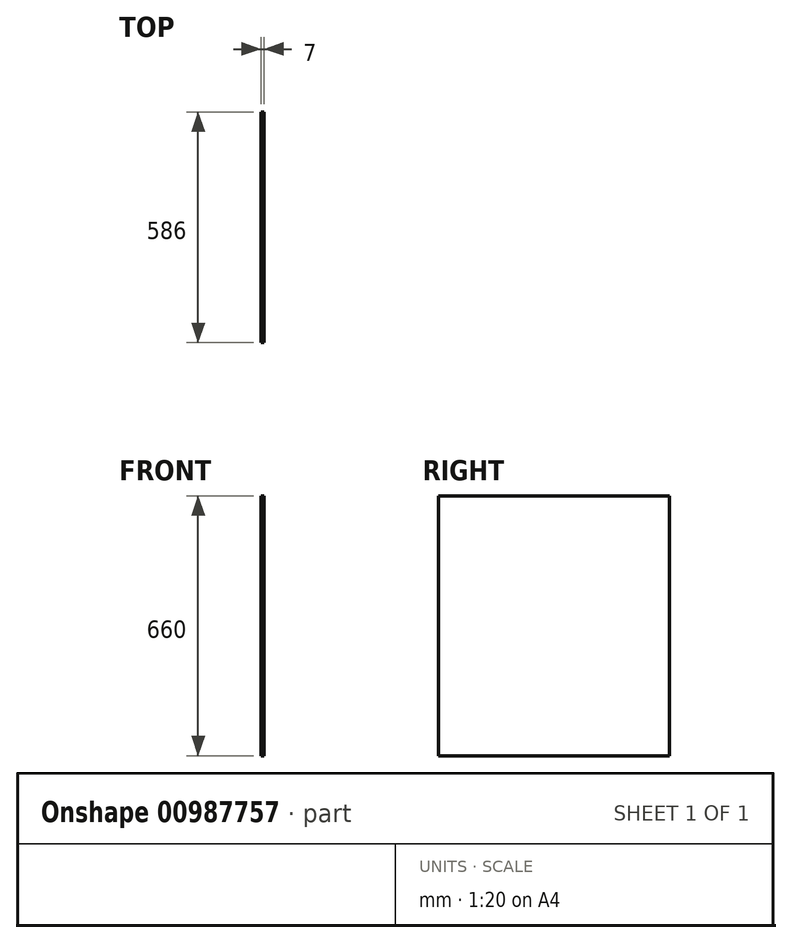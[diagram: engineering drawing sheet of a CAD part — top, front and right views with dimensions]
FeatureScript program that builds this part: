
annotation { "Feature Type Name" : "Feature", "Feature Type Description" : "" }
export const myFeature = defineFeature(function(context is Context, id is Id, definition is map)
    precondition{}
    {
        {
            var Q0;
            Q0=qCreatedBy(makeId("Right.planeOp"),FACE);
            var sketch = newSketch(context, id + "F0", { "sketchPlane" : qUnion([Q0])});
            skLineSegment(sketch, "E0.bottom", {"start": v(-293, -330) * mm, "end": v(293, -330) * mm});
            skLineSegment(sketch, "E0.top", {"start": v(-293, 330) * mm, "end": v(293, 330) * mm});
            skLineSegment(sketch, "E0.left", {"start": v(-293, -330) * mm, "end": v(-293, 330) * mm});
            skLineSegment(sketch, "E0.right", {"start": v(293, -330) * mm, "end": v(293, 330) * mm});
            skPoint(sketch, "E0.middle", {"position": v(0, 0) * mm});
            skSolve(sketch);
        }
        {
            var Q0;
            Q0=makeQuery(id+"F0.imprint","IMPRINT",FACE,{"disambiguationData":[TD([[makeQuery(id+"F0.imprint","IMPRINT",EDGE,{"derivedFrom":sQuery(id+"F0.wireOp",EDGE,"E0.bottom")}),1.0]])]});
            extrude(context, id + "F1", {"entities" : qUnion([Q0]), "depth" : 7 * mm, "offsetDistance" : 25 * mm});
        }
    });
